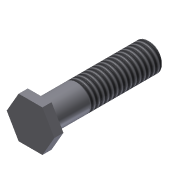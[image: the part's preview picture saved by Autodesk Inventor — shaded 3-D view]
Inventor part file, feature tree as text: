
AUTODESK INVENTOR PART (.ipt)
format: ipt  version: 2011 (Build 150239000, 239)  size: 94,720 bytes
history: native  units: in
note: dims shown in document units (in); Inventor stores cm internally (conversion verified against a paired STEP export)
features: extrude x2, sketch x2, thread x1, chamfer x1
ambient origin geometry x8: Origin, YZ Plane, XZ Plane, XY Plane, X Axis, Y Axis, Z Axis, Center Point
bodies: Solid1 (feature_tree)
feature tree (6):
  extrude  "Extrusion1"  Depth=1.5in TaperAngle=0.0deg
  extrude  "Extrusion2"  Depth=0.125in TaperAngle=0.0deg
  thread  "Thread1"  [1 undecoded]
  chamfer  "Chamfer1"  Distance=0.02in Angle=45.0deg
  sketch  "Sketch1"  dims[d0=0.375in d1=1.5in d2=0.0in]
  sketch  "Sketch2"  dims[d3=0.5625in d4=0.125in d5=0.0in d6=1.0in d7=0.0in d8=0.02in d9=0.125in d10=45.0deg]
note: 1 required parameter value undecoded (feature->parameter linkage not recoverable at this tier; creation-order binding heuristic only, values carry confidence <= 0.55)
